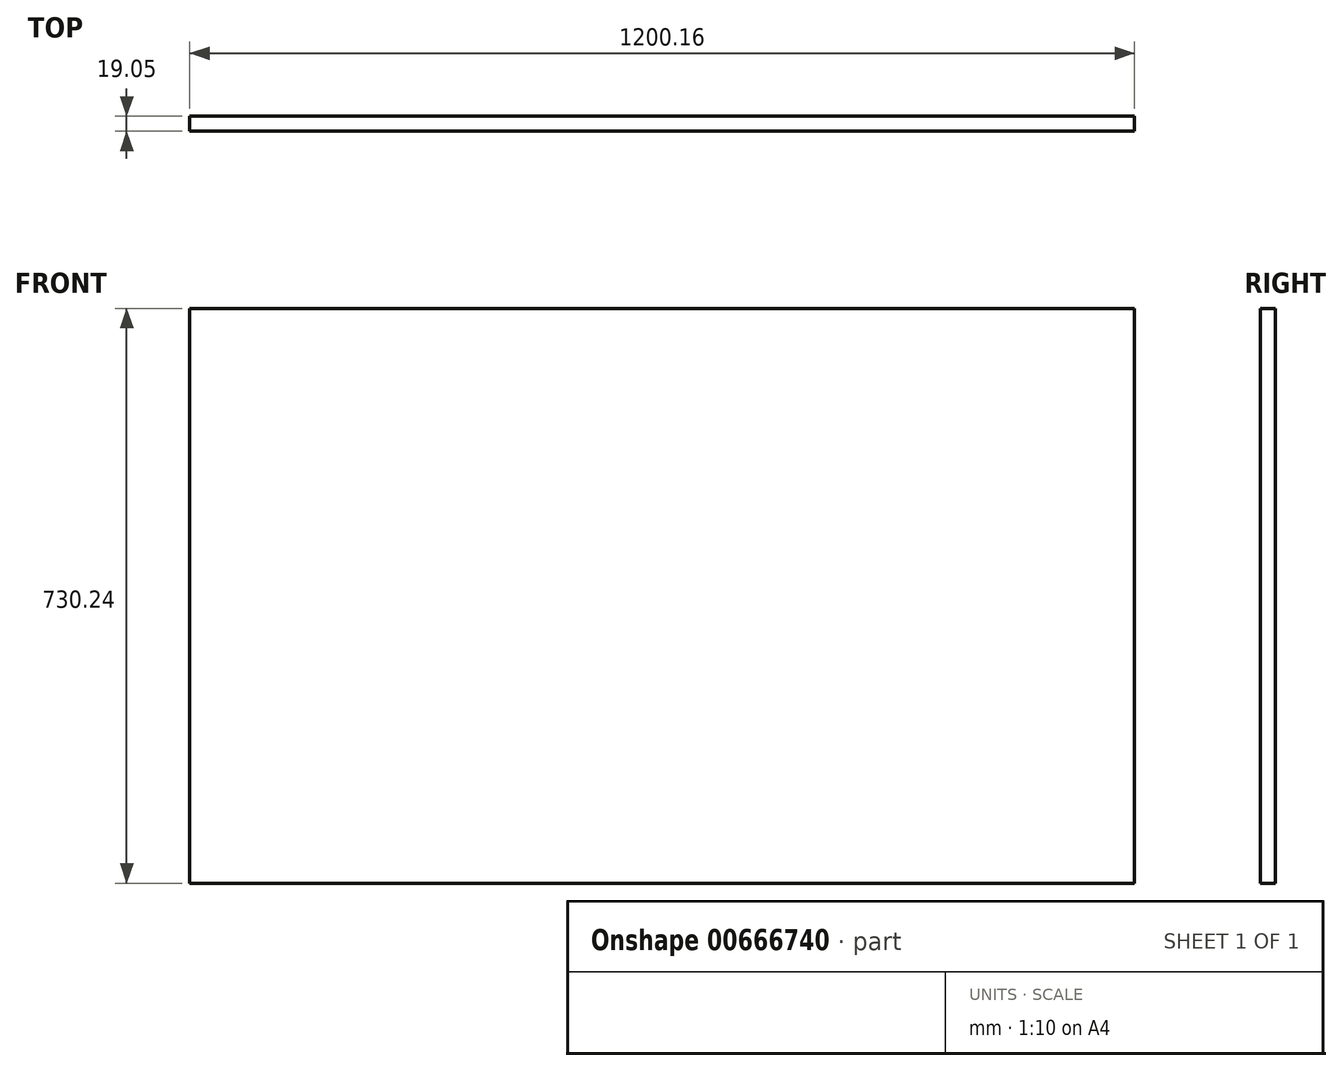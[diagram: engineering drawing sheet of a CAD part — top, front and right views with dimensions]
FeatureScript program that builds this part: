
annotation { "Feature Type Name" : "Feature", "Feature Type Description" : "" }
export const myFeature = defineFeature(function(context is Context, id is Id, definition is map)
    precondition{}
    {
        {
            var Q0;
            Q0=qCreatedBy(makeId("Front.planeOp"),FACE);
            var sketch = newSketch(context, id + "F0", { "sketchPlane" : qUnion([Q0])});
            skLineSegment(sketch, "E0.bottom", {"start": v(-600.08, 365.12) * mm, "end": v(600.08, 365.12) * mm});
            skLineSegment(sketch, "E0.top", {"start": v(-600.08, -365.13) * mm, "end": v(600.07, -365.13) * mm});
            skLineSegment(sketch, "E0.left", {"start": v(-600.08, 365.12) * mm, "end": v(-600.08, -365.13) * mm});
            skLineSegment(sketch, "E0.right", {"start": v(600.08, 365.12) * mm, "end": v(600.07, -365.13) * mm});
            skPoint(sketch, "E0.middle", {"position": v(0, 0) * mm});
            skSolve(sketch);
        }
        {
            var Q0;
            Q0=makeQuery(id+"F0.imprint","IMPRINT",FACE,{"disambiguationData":[TD([[makeQuery(id+"F0.imprint","IMPRINT",EDGE,{"derivedFrom":sQuery(id+"F0.wireOp",EDGE,"E0.bottom")}),-1.0]])]});
            extrude(context, id + "F1", {"entities" : qUnion([Q0]), "depth" : 19.05 * mm, "offsetDistance" : 25.4 * mm});
        }
    });
